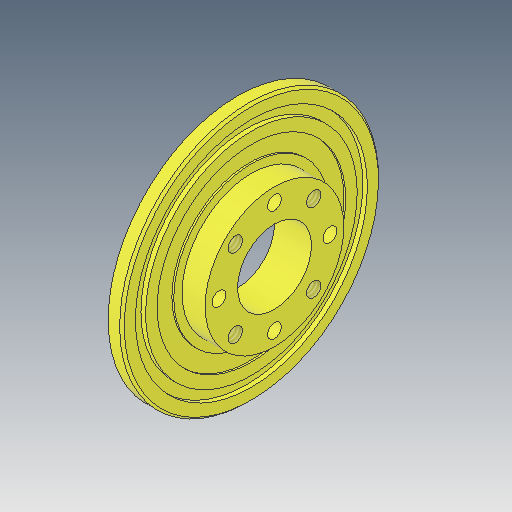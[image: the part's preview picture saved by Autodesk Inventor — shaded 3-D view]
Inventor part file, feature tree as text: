
AUTODESK INVENTOR PART (.ipt)
format: ipt  version: 2019.4 (Build 234330000, 330)  size: 182,784 bytes
history: native  units: mm
features: sketch x6, extrude x4, hole x2, other x1, chamfer x1
ambient origin geometry x8: Origin, YZ Plane, XZ Plane, XY Plane, X Axis, Y Axis, Z Axis, Center Point
bodies: Body1 (feature_tree)
feature tree (14):
  other  "ソリッド1"
  extrude  "押し出し1"  Depth=8.0mm
  extrude  "押し出し2"  Depth=28.0mm
  hole  "穴1"  [1 undecoded]
  hole  "穴2"  [1 undecoded]
  extrude  "押し出し3"  Depth=2.5mm TaperAngle=0.0deg
  extrude  "押し出し4"  Depth=12.0mm
  chamfer  "面取り1"  Distance=40.0mm Angle=360.0deg
  sketch  "スケッチ1"
  sketch  "スケッチ2"
  sketch  "スケッチ3"
  sketch  "スケッチ4"
  sketch  "スケッチ7"
  sketch  "スケッチ8"
note: 2 required parameter values undecoded (feature->parameter linkage not recoverable at this tier; creation-order binding heuristic only, values carry confidence <= 0.55)
